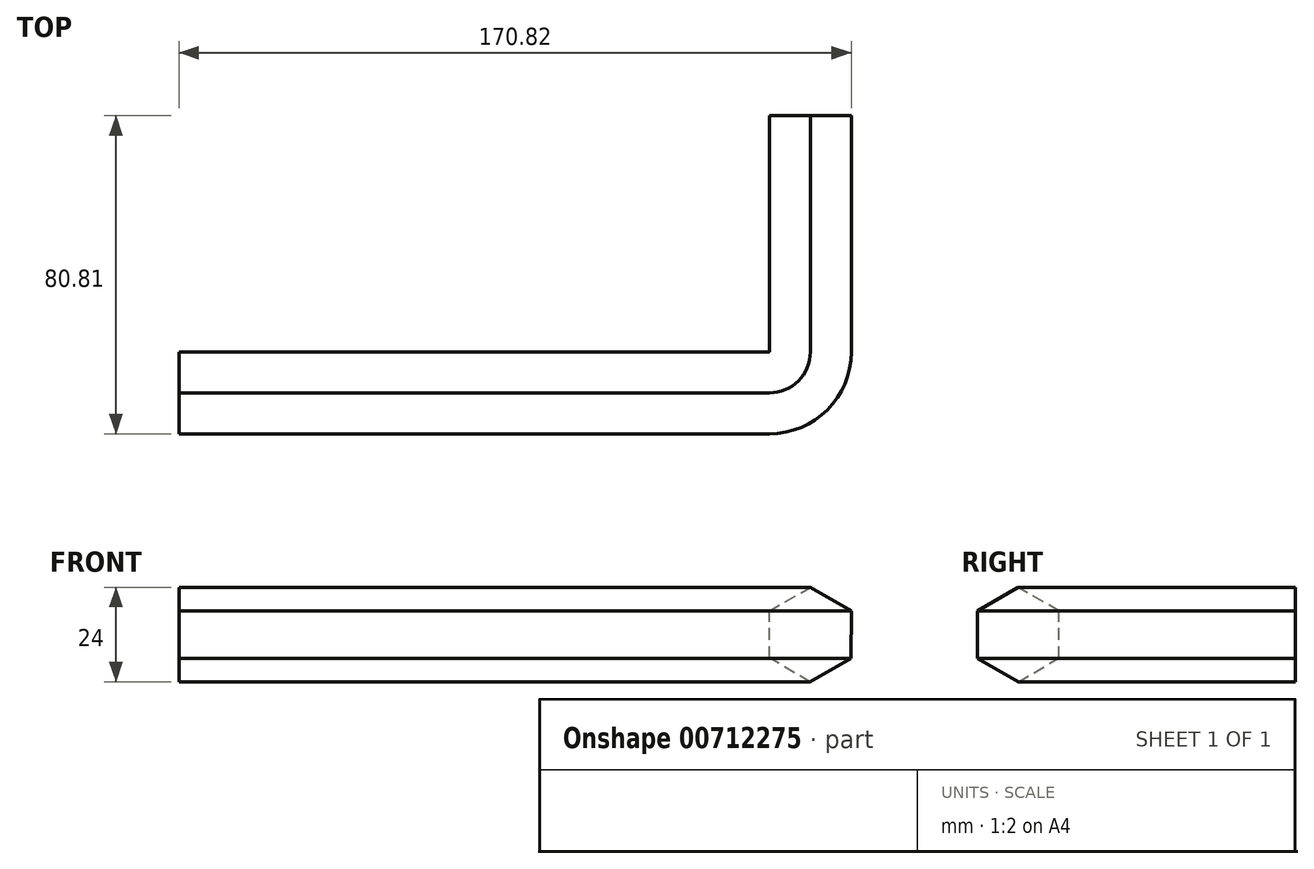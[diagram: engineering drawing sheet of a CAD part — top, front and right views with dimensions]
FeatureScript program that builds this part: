
annotation { "Feature Type Name" : "Feature", "Feature Type Description" : "" }
export const myFeature = defineFeature(function(context is Context, id is Id, definition is map)
    precondition{}
    {
        {
            var Q0;
            Q0=qCreatedBy(makeId("Front.planeOp"),FACE);
            var sketch = newSketch(context, id + "F0", { "sketchPlane" : qUnion([Q0])});
            skCircle(sketch, "E0.cCircle", {"center": v(0, 0) * mm, "radius": 10.4 * mm, "construction": true});
            skLineSegment(sketch, "E0.0", {"start": v(10.38, -6.02) * mm, "end": v(-0.03, -12) * mm});
            skLineSegment(sketch, "E0.1", {"start": v(-0.03, -12) * mm, "end": v(-10.4, -5.98) * mm});
            skLineSegment(sketch, "E0.2", {"start": v(-10.4, -5.98) * mm, "end": v(-10.38, 6.02) * mm});
            skLineSegment(sketch, "E0.3", {"start": v(-10.38, 6.02) * mm, "end": v(0.03, 12) * mm});
            skLineSegment(sketch, "E0.4", {"start": v(0.03, 12) * mm, "end": v(10.4, 5.98) * mm});
            skLineSegment(sketch, "E0.5", {"start": v(10.4, 5.98) * mm, "end": v(10.38, -6.02) * mm});
            skLineSegment(sketch, "E1", {"start": v(-10.4, -5.98) * mm, "end": v(-10.4, 23.04) * mm});
            skSolve(sketch);
        }
        {
            var Q0;
            Q0=makeQuery(id+"F0.imprint","IMPRINT",FACE,{"disambiguationData":[TD([[makeQuery(id+"F0.imprint","IMPRINT",EDGE,{"derivedFrom":sQuery(id+"F0.wireOp",EDGE,"E0.0")}),-1.0]])]});
            var Q1;
            Q1=sQuery(id+"F0.wireOp",EDGE,"E1");
            revolve(context, id + "F1", {"surfaceOperationType" : NewSurfaceOperationType.NEW, "entities" : qUnion([Q0]), "axis" : qUnion([Q1]), "revolveType" : RevolveType.ONE_DIRECTION, "oppositeDirection" : true, "angle" : 90 * degree});
        }
        {
            var Q0;
            Q0 = qSketchRegion(id + "F0", true);
            extrude(context, id + "F2", {"entities" : qUnion([Q0]), "operationType" : NewBodyOperationType.ADD, "oppositeDirection" : true, "depth" : 60 * mm, "offsetDistance" : 25 * mm});
        }
        {
            var Q0;
            Q0=makeQuery(id+"F1.opRevolve","CAP_FACE",FACE,{"disambiguationData":[OSD([sQuery(id+"F0.wireOp",EDGE,"E0.0"),sQuery(id+"F0.wireOp",EDGE,"E0.1"),sQuery(id+"F0.wireOp",EDGE,"E0.2"),sQuery(id+"F0.wireOp",EDGE,"E0.3"),sQuery(id+"F0.wireOp",EDGE,"E0.4"),sQuery(id+"F0.wireOp",EDGE,"E0.5")])],"isStart":false});
            var sketch = newSketch(context, id + "F3", { "sketchPlane" : qUnion([Q0])});
            skSolve(sketch);
        }
        {
            var Q0;
            Q0=makeQuery(id+"F3.imprint","IMPRINT",FACE,{"disambiguationData":[TD([[makeQuery(id+"F3.imprint","IMPRINT",EDGE,{"derivedFrom":makeQuery(id+"F1.opRevolve","CAP_EDGE",EDGE,{"disambiguationData":[OSD([sQuery(id+"F0.wireOp",EDGE,"E0.0")])],"isStart":false})}),-1.0]])]});
            extrude(context, id + "F4", {"entities" : qUnion([Q0]), "operationType" : NewBodyOperationType.ADD, "depth" : 150 * mm, "offsetDistance" : 25 * mm});
        }
    });
